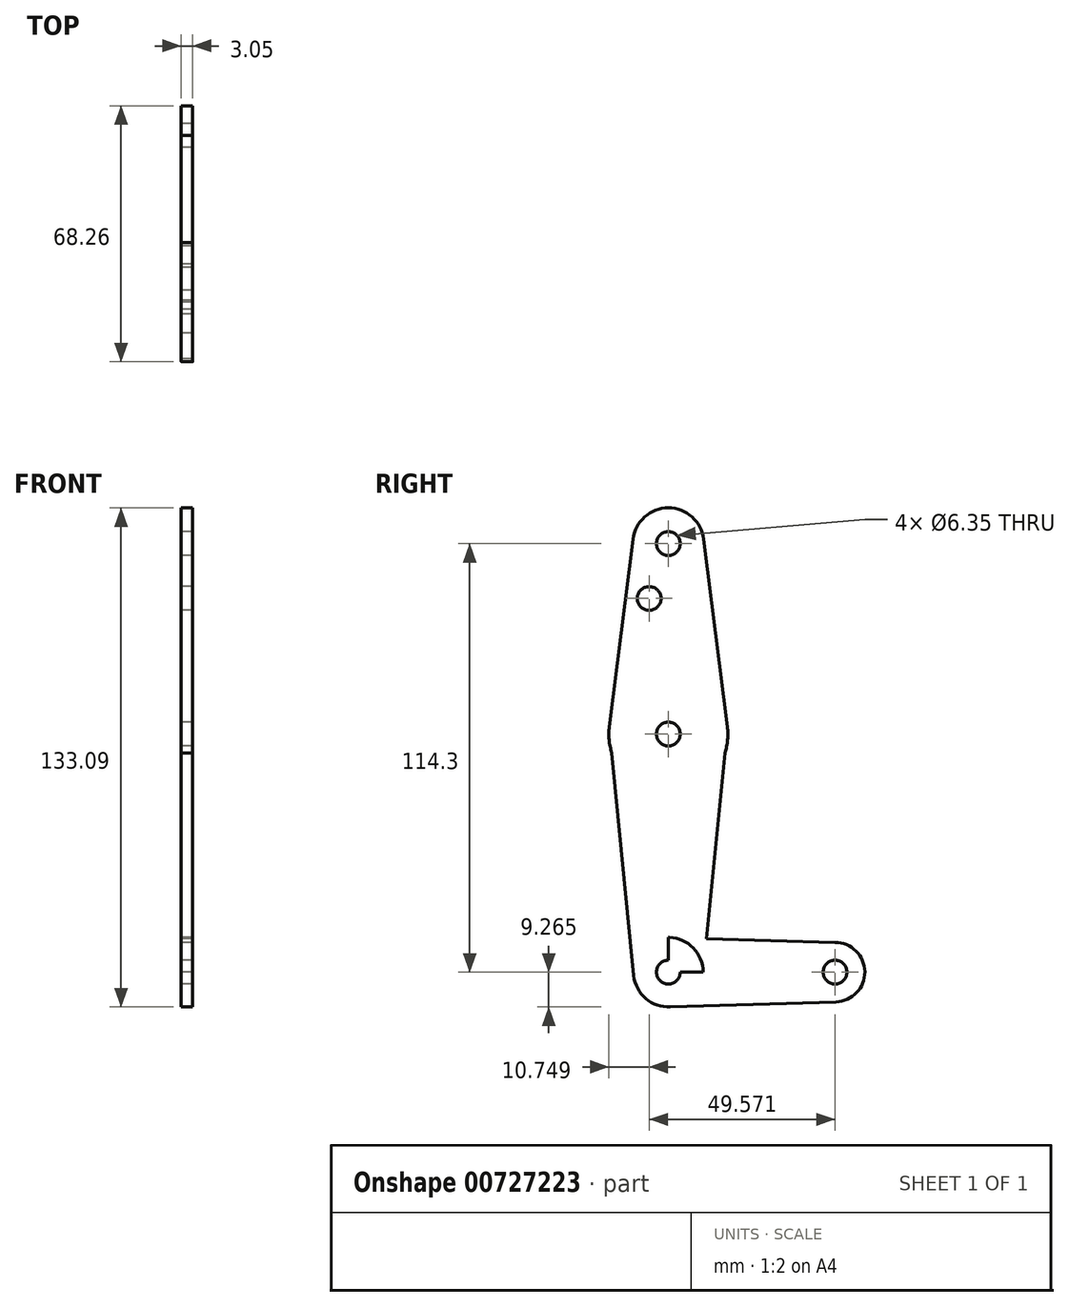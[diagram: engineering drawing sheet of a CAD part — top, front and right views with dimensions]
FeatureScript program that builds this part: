
annotation { "Feature Type Name" : "Feature", "Feature Type Description" : "" }
export const myFeature = defineFeature(function(context is Context, id is Id, definition is map)
    precondition{}
    {
        {
            var Q0;
            Q0=qCreatedBy(makeId("Right.planeOp"),FACE);
            var sketch = newSketch(context, id + "F0", { "sketchPlane" : qUnion([Q0])});
            skCircle(sketch, "E0", {"center": v(0, 81.72) * mm, "radius": 9.53 * mm});
            skLineSegment(sketch, "E1", {"start": v(0, 81.72) * mm, "end": v(0, 30.92) * mm});
            skArc(sketch, "E2", {"start": v(3.52, 46.4) * mm, "mid": v(-4.16, 15.6) * mm, "end": v(4.79, 46.05) * mm});
            skLineSegment(sketch, "E3", {"start": v(0, 30.92) * mm, "end": v(0, -32.58) * mm});
            skCircle(sketch, "E4", {"center": v(0, -32.58) * mm, "radius": 9.26 * mm});
            skLineSegment(sketch, "E5", {"start": v(0, -32.58) * mm, "end": v(44.45, -32.58) * mm});
            skCircle(sketch, "E6", {"center": v(44.45, -32.58) * mm, "radius": 7.94 * mm});
            skLineSegment(sketch, "E7", {"start": v(9.45, 82.9) * mm, "end": v(15.75, 32.9) * mm});
            skLineSegment(sketch, "E8", {"start": v(-9.45, 82.9) * mm, "end": v(-15.75, 32.9) * mm});
            skLineSegment(sketch, "E9", {"start": v(-15.75, 32.9) * mm, "end": v(-9.22, -33.5) * mm});
            skLineSegment(sketch, "E10", {"start": v(15.75, 32.9) * mm, "end": v(9.3, -32.58) * mm});
            skLineSegment(sketch, "E11", {"start": v(44.45, -24.65) * mm, "end": v(0, -23.32) * mm});
            skLineSegment(sketch, "E12", {"start": v(0, -41.85) * mm, "end": v(44.69, -40.52) * mm});
            skCircle(sketch, "E13", {"center": v(0, 81.72) * mm, "radius": 3.18 * mm});
            skCircle(sketch, "E14", {"center": v(0, 30.92) * mm, "radius": 3.18 * mm});
            skCircle(sketch, "E15", {"center": v(0, -32.58) * mm, "radius": 3.18 * mm});
            skCircle(sketch, "E16", {"center": v(44.45, -32.58) * mm, "radius": 3.18 * mm});
            skCircle(sketch, "E17", {"center": v(-5.12, 67.08) * mm, "radius": 3.18 * mm});
            skSolve(sketch);
        }
        {
            var Q0;
            Q0 = qSketchRegion(id + "F0", true);
            extrude(context, id + "F1", {"entities" : qUnion([Q0]), "depth" : 3.05 * mm, "offsetDistance" : 25.4 * mm});
        }
    });
